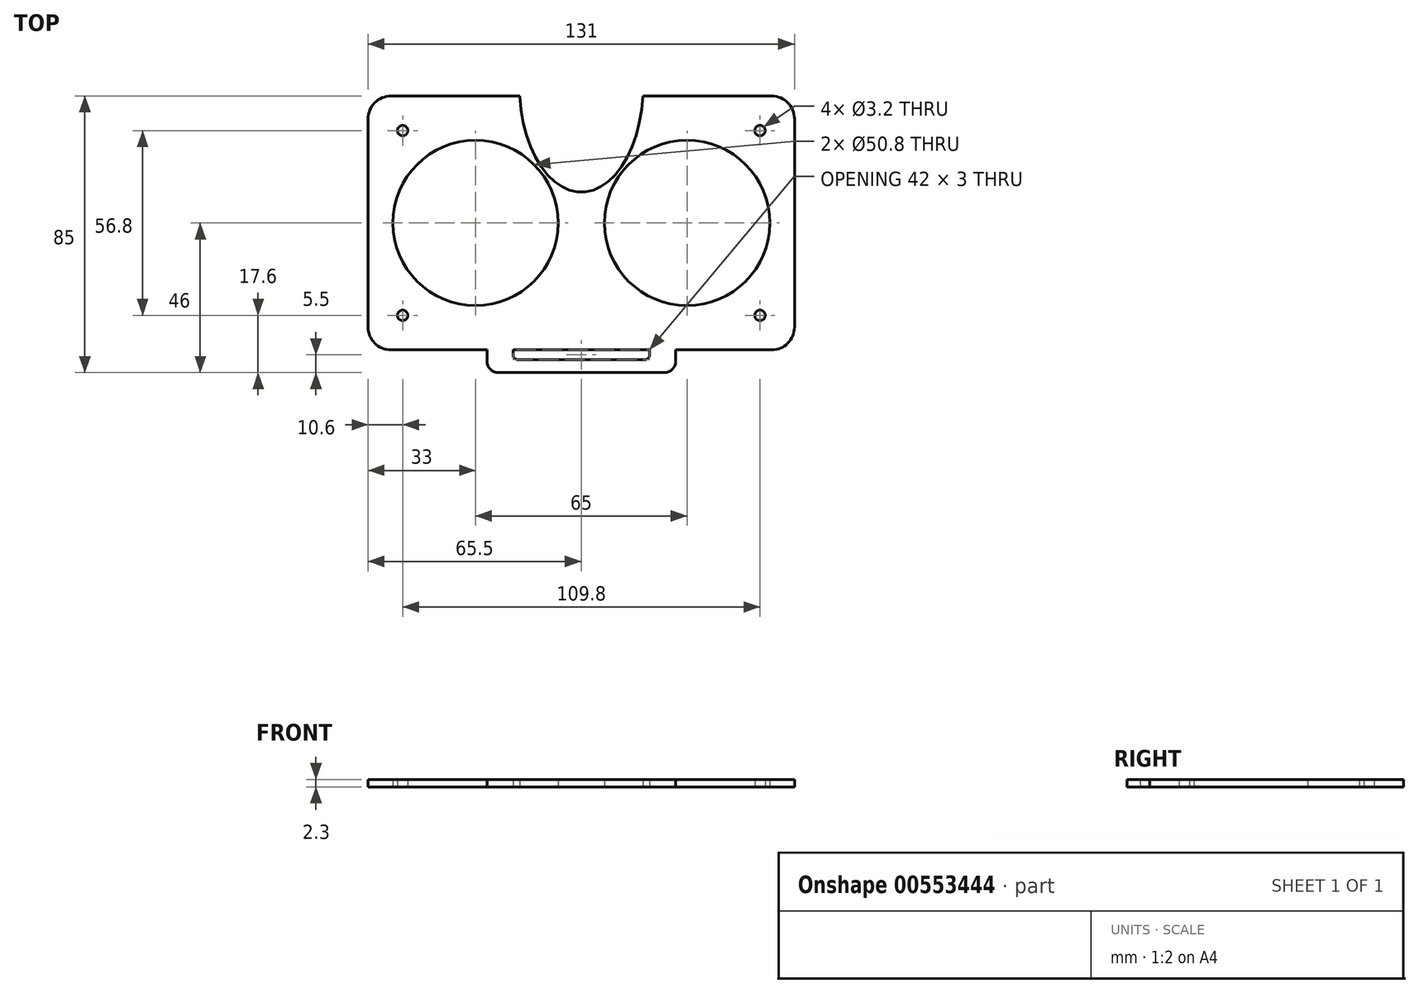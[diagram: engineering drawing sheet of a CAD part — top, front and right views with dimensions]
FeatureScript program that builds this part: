
annotation { "Feature Type Name" : "Feature", "Feature Type Description" : "" }
export const myFeature = defineFeature(function(context is Context, id is Id, definition is map)
    precondition{}
    {
        {
            var Q0;
            Q0=qCreatedBy(makeId("Top.planeOp"),FACE);
            var sketch = newSketch(context, id + "F0", { "sketchPlane" : qUnion([Q0])});
            skCircle(sketch, "E0", {"center": v(-32.5, 0) * mm, "radius": 25.4 * mm});
            skCircle(sketch, "E1", {"center": v(32.5, 0) * mm, "radius": 25.4 * mm});
            skCircle(sketch, "E2", {"center": v(32.5, 0) * mm, "radius": 24.5 * mm});
            skCircle(sketch, "E3", {"center": v(-32.5, 0) * mm, "radius": 24.5 * mm});
            skLineSegment(sketch, "E4.bottom", {"start": v(60.5, 34) * mm, "end": v(-60.5, 34) * mm});
            skLineSegment(sketch, "E4.top", {"start": v(60.5, -34) * mm, "end": v(-60.5, -34) * mm});
            skLineSegment(sketch, "E4.left", {"start": v(60.5, 34) * mm, "end": v(60.5, -34) * mm});
            skLineSegment(sketch, "E4.right", {"start": v(-60.5, 34) * mm, "end": v(-60.5, -34) * mm});
            skPoint(sketch, "E4.middle", {"position": v(0, 0) * mm});
            skCircle(sketch, "E5", {"center": v(-54.9, 28.4) * mm, "radius": 1.6 * mm});
            skCircle(sketch, "E6", {"center": v(-54.9, -28.4) * mm, "radius": 1.6 * mm});
            skCircle(sketch, "E7", {"center": v(54.9, -28.4) * mm, "radius": 1.6 * mm});
            skCircle(sketch, "E8", {"center": v(54.9, 28.4) * mm, "radius": 1.6 * mm});
            skSolve(sketch);
        }
        {
            var Q0;
            Q0=qCreatedBy(makeId("Top.planeOp"),FACE);
            var sketch = newSketch(context, id + "F1", { "sketchPlane" : qUnion([Q0])});
            skLineSegment(sketch, "E9.bottom", {"start": v(60.5, 34) * mm, "end": v(-60.5, 34) * mm});
            skLineSegment(sketch, "E9.top", {"start": v(60.5, -34) * mm, "end": v(-60.5, -34) * mm});
            skLineSegment(sketch, "E9.left", {"start": v(60.5, 34) * mm, "end": v(60.5, -34) * mm});
            skLineSegment(sketch, "E9.right", {"start": v(-60.5, 34) * mm, "end": v(-60.5, -34) * mm});
            skPoint(sketch, "E9.middle", {"position": v(0, 0) * mm});
            skLineSegment(sketch, "E10.bottom", {"start": v(65.5, -39) * mm, "end": v(-65.5, -39) * mm});
            skLineSegment(sketch, "E10.top", {"start": v(65.5, 39) * mm, "end": v(-65.5, 39) * mm});
            skLineSegment(sketch, "E10.left", {"start": v(65.5, -39) * mm, "end": v(65.5, 39) * mm});
            skLineSegment(sketch, "E10.right", {"start": v(-65.5, -39) * mm, "end": v(-65.5, 39) * mm});
            skLineSegment(sketch, "E11.bottom", {"start": v(-29, -46) * mm, "end": v(29, -46) * mm});
            skLineSegment(sketch, "E11.top", {"start": v(-29, -32) * mm, "end": v(29, -32) * mm});
            skLineSegment(sketch, "E11.left", {"start": v(-29, -46) * mm, "end": v(-29, -32) * mm});
            skLineSegment(sketch, "E11.right", {"start": v(29, -46) * mm, "end": v(29, -32) * mm});
            skPoint(sketch, "E11.middle", {"position": v(0, -39) * mm});
            skLineSegment(sketch, "E12.bottom", {"start": v(21, -42) * mm, "end": v(-21, -42) * mm});
            skLineSegment(sketch, "E12.top", {"start": v(21, -36) * mm, "end": v(-21, -36) * mm});
            skLineSegment(sketch, "E12.left", {"start": v(21, -42) * mm, "end": v(21, -36) * mm});
            skLineSegment(sketch, "E12.right", {"start": v(-21, -42) * mm, "end": v(-21, -36) * mm});
            skSolve(sketch);
        }
        {
            var Q0;
            Q0=makeQuery(id+"F1.imprint","IMPRINT",FACE,{"disambiguationData":[TD([[makeQuery(id+"F1.imprint","IMPRINT",EDGE,{"derivedFrom":sQuery(id+"F1.wireOp",EDGE,"E9.bottom")}),-1.0]])]});
            var sketch = newSketch(context, id + "F2", { "sketchPlane" : qUnion([Q0])});
            skEllipse(sketch, "E13", {"center": v(0, 42) * mm, "majorRadius": 32.5 * mm, "minorRadius": 19 * mm, "majorAxis": v(0, -1)});
            skSolve(sketch);
        }
        {
            var Q0;
            Q0=makeQuery(id+"F2.imprint","IMPRINT",FACE,{"disambiguationData":[TD([[makeQuery(id+"F2.imprint","IMPRINT",EDGE,{"derivedFrom":makeQuery(id+"F1.imprint","IMPRINT",EDGE,{"derivedFrom":sQuery(id+"F1.wireOp",EDGE,"E9.top")})}),1.0]])]});
            var Q1;
            Q1=makeQuery(id+"F0.imprint","IMPRINT",FACE,{"disambiguationData":[TD([[makeQuery(id+"F0.imprint","IMPRINT",EDGE,{"derivedFrom":sQuery(id+"F0.wireOp",EDGE,"E0")}),-1.0]])]});
            extrude(context, id + "F3", {"entities" : qUnion([Q0, Q1]), "depth" : 2.3 * mm, "offsetDistance" : 25 * mm});
        }
        {
            var Q0;
            Q0 = qSketchRegion(id + "F2", true);
            extrude(context, id + "F4", {"entities" : qUnion([Q0]), "operationType" : NewBodyOperationType.REMOVE, "depth" : 25 * mm, "offsetDistance" : 25 * mm});
        }
        {
            var Q0;
            Q0=makeQuery(id+"F3.opExtrude","SWEPT_BODY",BODY,{"disambiguationData":[OSD([sQuery(id+"F0.wireOp",EDGE,"E0"),sQuery(id+"F0.wireOp",EDGE,"E1"),sQuery(id+"F0.wireOp",EDGE,"E4.bottom"),sQuery(id+"F0.wireOp",EDGE,"E4.top"),sQuery(id+"F0.wireOp",EDGE,"E4.left"),sQuery(id+"F0.wireOp",EDGE,"E4.right")])]});
            var Q1;
            Q1=makeQuery(id+"F3.opExtrude","SWEPT_BODY",BODY,{"disambiguationData":[OSD([sQuery(id+"F1.wireOp",EDGE,"E9.bottom"),sQuery(id+"F1.wireOp",EDGE,"E9.top"),sQuery(id+"F1.wireOp",EDGE,"E9.left"),sQuery(id+"F1.wireOp",EDGE,"E9.right"),sQuery(id+"F1.wireOp",EDGE,"E10.bottom"),sQuery(id+"F1.wireOp",EDGE,"E10.top"),sQuery(id+"F1.wireOp",EDGE,"E10.left"),sQuery(id+"F1.wireOp",EDGE,"E10.right"),sQuery(id+"F2.wireOp",EDGE,"E13")])]});
            booleanBodies(context, id + "F5", {"operationType" : BooleanOperationType.UNION, "tools" : qUnion([Q0, Q1])});
        }
        {
            var Q0;
            {var subQ12=sQuery(id+"F1.wireOp",EDGE,"E12.top");Q0=makeQuery(id+"F1.imprint","IMPRINT",FACE,{"disambiguationData":[TD([[makeQuery(id+"F1.imprint","IMPRINT",EDGE,{"derivedFrom":subQ12}),-1.0]])]});}
            var Q1;
            {var subQ1=sQuery(id+"F1.wireOp",EDGE,"E11.bottom");Q1=makeQuery(id+"F1.imprint","IMPRINT",FACE,{"disambiguationData":[TD([[makeQuery(id+"F1.imprint","IMPRINT",EDGE,{"derivedFrom":subQ1}),1.0]])]});}
            var Q2;
            {var subQ0=sQuery(id+"F2.wireOp",EDGE,"E13");var subQ1=sQuery(id+"F1.wireOp",EDGE,"E10.top");var subQ2=sQuery(id+"F1.wireOp",EDGE,"E10.bottom");var subQ3=sQuery(id+"F1.wireOp",EDGE,"E9.top");var subQ4=sQuery(id+"F1.wireOp",EDGE,"E9.bottom");Q2=makeQuery(id+"F5.opBoolean","MERGE",FACE,{"derivedFrom":[makeQuery(id+"F3.opExtrude","CAP_FACE",FACE,{"disambiguationData":[OSD([subQ4,subQ3,sQuery(id+"F1.wireOp",EDGE,"E9.left"),subQ2,subQ1,sQuery(id+"F1.wireOp",EDGE,"E10.left"),sQuery(id+"F1.wireOp",EDGE,"E11.right"),subQ0])],"isStart":false}),makeQuery(id+"F3.opExtrude","CAP_FACE",FACE,{"disambiguationData":[OSD([subQ4,subQ3,sQuery(id+"F1.wireOp",EDGE,"E9.right"),subQ2,subQ1,sQuery(id+"F1.wireOp",EDGE,"E10.right"),sQuery(id+"F1.wireOp",EDGE,"E11.left"),subQ0])],"isStart":false}),makeQuery(id+"F3.opExtrude","CAP_FACE",FACE,{"disambiguationData":[OSD([sQuery(id+"F0.wireOp",EDGE,"E0"),sQuery(id+"F0.wireOp",EDGE,"E1"),sQuery(id+"F0.wireOp",EDGE,"E4.bottom"),sQuery(id+"F0.wireOp",EDGE,"E4.top"),sQuery(id+"F0.wireOp",EDGE,"E4.left"),sQuery(id+"F0.wireOp",EDGE,"E4.right")])],"isStart":false})]});}
            extrude(context, id + "F6", {"entities" : qUnion([Q0, Q1]), "operationType" : NewBodyOperationType.ADD, "endBound" : BoundingType.UP_TO_SURFACE, "depth" : 25 * mm, "endBoundEntityFace" : qUnion([Q2]), "offsetDistance" : 25 * mm});
        }
        {
            var Q0;
            {var subQ5=sQuery(id+"F1.wireOp",EDGE,"E12.top");Q0=makeQuery(id+"F1.imprint","IMPRINT",FACE,{"disambiguationData":[TD([[makeQuery(id+"F1.imprint","IMPRINT",EDGE,{"derivedFrom":subQ5}),1.0]])]});}
            var Q1;
            {var subQ0=sQuery(id+"F2.wireOp",EDGE,"E13");var subQ1=sQuery(id+"F1.wireOp",EDGE,"E11.right");var subQ2=sQuery(id+"F1.wireOp",EDGE,"E11.left");var subQ3=sQuery(id+"F1.wireOp",EDGE,"E10.right");var subQ4=sQuery(id+"F1.wireOp",EDGE,"E10.left");var subQ5=sQuery(id+"F1.wireOp",EDGE,"E10.top");var subQ6=sQuery(id+"F1.wireOp",EDGE,"E10.bottom");var subQ7=sQuery(id+"F1.wireOp",EDGE,"E9.right");var subQ8=sQuery(id+"F1.wireOp",EDGE,"E9.left");var subQ9=sQuery(id+"F1.wireOp",EDGE,"E9.top");var subQ10=sQuery(id+"F1.wireOp",EDGE,"E9.bottom");var subQ11=sQuery(id+"F0.wireOp",EDGE,"E4.right");var subQ12=sQuery(id+"F0.wireOp",EDGE,"E4.left");var subQ13=sQuery(id+"F0.wireOp",EDGE,"E4.top");var subQ14=sQuery(id+"F0.wireOp",EDGE,"E4.bottom");var subQ15=sQuery(id+"F0.wireOp",EDGE,"E1");var subQ16=sQuery(id+"F0.wireOp",EDGE,"E0");Q1=makeQuery(id+"F6.boolean.opBoolean","MERGE",FACE,{"derivedFrom":[makeQuery(id+"F5.opBoolean","MERGE",FACE,{"derivedFrom":[makeQuery(id+"F3.opExtrude","CAP_FACE",FACE,{"disambiguationData":[OSD([subQ10,subQ9,subQ8,subQ6,subQ5,subQ4,subQ1,subQ0])],"isStart":false}),makeQuery(id+"F3.opExtrude","CAP_FACE",FACE,{"disambiguationData":[OSD([subQ10,subQ9,subQ7,subQ6,subQ5,subQ3,subQ2,subQ0])],"isStart":false}),makeQuery(id+"F3.opExtrude","CAP_FACE",FACE,{"disambiguationData":[OSD([subQ16,subQ15,subQ14,subQ13,subQ12,subQ11])],"isStart":false})]}),makeQuery(id+"F6.opExtrude","CAP_FACE",FACE,{"disambiguationData":[OSD([subQ16,subQ15,subQ14,subQ13,subQ12,subQ11,subQ10,subQ9,subQ8,subQ7,subQ6,subQ5,subQ4,subQ3,subQ2,subQ1,subQ0])],"isStart":false})]});}
            extrude(context, id + "F7", {"entities" : qUnion([Q0]), "operationType" : NewBodyOperationType.ADD, "endBound" : BoundingType.UP_TO_SURFACE, "depth" : 25 * mm, "endBoundEntityFace" : qUnion([Q1]), "offsetDistance" : 25 * mm});
        }
        {
            var Q0;
            Q0=makeQuery(id+"F3.opExtrude","SWEPT_EDGE",EDGE,{"disambiguationData":[OSD([sQuery(id+"F1.wireOp",EDGE,"E10.bottom"),sQuery(id+"F1.wireOp",EDGE,"E10.left")])]});
            var Q1;
            Q1=makeQuery(id+"F3.opExtrude","SWEPT_EDGE",EDGE,{"disambiguationData":[OSD([sQuery(id+"F1.wireOp",EDGE,"E10.top"),sQuery(id+"F1.wireOp",EDGE,"E10.left")])]});
            var Q2;
            Q2=makeQuery(id+"F3.opExtrude","SWEPT_EDGE",EDGE,{"disambiguationData":[OSD([sQuery(id+"F1.wireOp",EDGE,"E10.top"),sQuery(id+"F1.wireOp",EDGE,"E10.right")])]});
            var Q3;
            Q3=makeQuery(id+"F3.opExtrude","SWEPT_EDGE",EDGE,{"disambiguationData":[OSD([sQuery(id+"F1.wireOp",EDGE,"E10.bottom"),sQuery(id+"F1.wireOp",EDGE,"E10.right")])]});
            fillet(context, id + "F8", {"entities" : qUnion([Q0, Q1, Q2, Q3]), "radius" : 7 * mm, "tangentPropagation" : true, "allowEdgeOverflow" : false});
        }
        {
            var Q0;
            Q0=makeQuery(id+"F3.opExtrude","SWEPT_EDGE",EDGE,{"disambiguationData":[OSD([sQuery(id+"F1.wireOp",EDGE,"E10.bottom"),sQuery(id+"F1.wireOp",EDGE,"E11.right")])]});
            var Q1;
            Q1=makeQuery(id+"F6.opExtrude","SWEPT_EDGE",EDGE,{"disambiguationData":[OSD([sQuery(id+"F1.wireOp",EDGE,"E11.bottom"),sQuery(id+"F1.wireOp",EDGE,"E11.right")])]});
            var Q2;
            Q2=makeQuery(id+"F3.opExtrude","SWEPT_EDGE",EDGE,{"disambiguationData":[OSD([sQuery(id+"F1.wireOp",EDGE,"E10.bottom"),sQuery(id+"F1.wireOp",EDGE,"E11.left")])]});
            var Q3;
            Q3=makeQuery(id+"F6.opExtrude","SWEPT_EDGE",EDGE,{"disambiguationData":[OSD([sQuery(id+"F1.wireOp",EDGE,"E11.bottom"),sQuery(id+"F1.wireOp",EDGE,"E11.left")])]});
            fillet(context, id + "F9", {"entities" : qUnion([Q0, Q1, Q2, Q3]), "radius" : 3.5 * mm, "tangentPropagation" : true, "allowEdgeOverflow" : false});
        }
        {
            var Q0;
            Q0=makeQuery(id+"F6.opExtrude","SWEPT_EDGE",EDGE,{"disambiguationData":[OSD([sQuery(id+"F1.wireOp",EDGE,"E12.bottom"),sQuery(id+"F1.wireOp",EDGE,"E12.right")])]});
            var Q1;
            Q1=makeQuery(id+"F7.opExtrude","SWEPT_EDGE",EDGE,{"disambiguationData":[OSD([sQuery(id+"F1.wireOp",EDGE,"E10.bottom"),sQuery(id+"F1.wireOp",EDGE,"E12.right")])]});
            var Q2;
            Q2=makeQuery(id+"F6.opExtrude","SWEPT_EDGE",EDGE,{"disambiguationData":[OSD([sQuery(id+"F1.wireOp",EDGE,"E12.bottom"),sQuery(id+"F1.wireOp",EDGE,"E12.left")])]});
            var Q3;
            Q3=makeQuery(id+"F7.opExtrude","SWEPT_EDGE",EDGE,{"disambiguationData":[OSD([sQuery(id+"F1.wireOp",EDGE,"E10.bottom"),sQuery(id+"F1.wireOp",EDGE,"E12.left")])]});
            fillet(context, id + "F10", {"entities" : qUnion([Q0, Q1, Q2, Q3]), "radius" : 1.5 * mm, "tangentPropagation" : true, "allowEdgeOverflow" : false});
        }
    });
